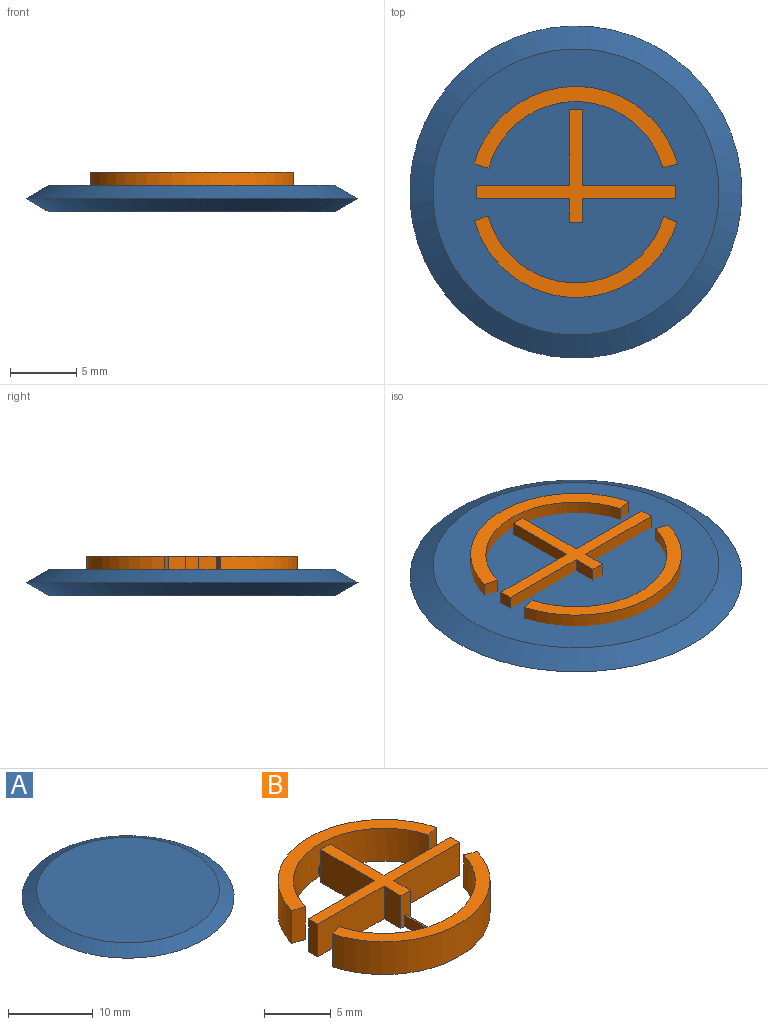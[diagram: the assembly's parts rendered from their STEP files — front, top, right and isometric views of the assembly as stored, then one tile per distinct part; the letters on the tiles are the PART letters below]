
ASSEMBLY  parts=2 mates=1
PART A: 4 faces, bbox 25x25x2 mm
  f0: plane 21.54x21.54mm, normal (0,0,1), area 364.3mm2, adj f1
  f1: cone r=12.5mm half-angle=60deg, axis (0,0,-1), area 146.2mm2, adj f0,f2
  f2: cone r=12.5mm half-angle=60deg, axis (0,0,1), area 146.2mm2, adj f1,f3
  f3: plane 21.54x21.54mm, normal (0,0,-1), area 364.3mm2, adj f2
PART B: 30 faces, bbox 15.3x15.9x3 mm
  f0: plane 1x0.59mm, normal (1,0,0), area 0.6mm2, adj f9,f25,f27,f28
  f1: plane 1x0.59mm, normal (-1,0,0), area 0.6mm2, adj f9,f25,f27,f28
  f2: plane 4.56x1mm, normal (-1,0,0), area 4.6mm2, adj f15,f16,f27,f29
  f3: plane 4.56x1mm, normal (1,0,0), area 4.6mm2, adj f15,f16,f27,f29
  f4: plane 15.25x6.11mm, normal (0,0,1), area 20.9mm2, adj f16,f17,f18,f19
  f5: plane 15x8.5mm, normal (0,0,1), area 22.5mm2, adj f10,f11,f12,f13,f14,f15,f20,f21
  f6: plane 3x1.12mm, normal (0.23,-0.97,0), area 3.4mm2, adj f7,f9,f26,f27
  f7: cylinder r=7.94mm len=15.32mm, axis (0,0,-1), area 62.1mm2, adj f6,f8,f26,f27
  f8: plane 3x1.1mm, normal (-0.27,-0.96,0), area 3.4mm2, adj f7,f9,f26,f27
  f9: cylinder r=6.8mm len=13.1mm, axis (0,0,-1), area 52.9mm2, adj f0,f1,f6,f8,f26,f27,f28
  f10: plane 5.71x3mm, normal (-1,0,0), area 17.1mm2, adj f5,f11,f25,f27
  f11: plane 7x3mm, normal (0,1,0), area 21mm2, adj f5,f10,f12,f27
  f12: plane 3x1mm, normal (-1,0,0), area 3mm2, adj f5,f11,f13,f27
  f13: plane 7x3mm, normal (0,-1,0), area 21mm2, adj f5,f12,f14,f27
  f14: plane 3x1.79mm, normal (-1,0,0), area 5.4mm2, adj f5,f13,f15,f27
  f15: plane 3x1mm, normal (0,-1,0), area 2.8mm2, adj f2,f3,f5,f14,f20,f27,f29
  f16: cylinder r=6.85mm len=13.19mm, axis (0,0,-1), area 53.2mm2, adj f2,f3,f4,f17,f19,f27,f29
  f17: plane 3x1.04mm, normal (-0.31,0.95,0), area 3.3mm2, adj f4,f16,f18,f27
  f18: cylinder r=7.94mm len=15.25mm, axis (0,0,-1), area 61.4mm2, adj f4,f17,f19,f27
  f19: plane 3x1.02mm, normal (0.37,0.93,0), area 3.3mm2, adj f4,f16,f18,f27
  f20: plane 3x1.79mm, normal (1,0,0), area 5.4mm2, adj f5,f15,f21,f27
  f21: plane 7x3mm, normal (0,-1,0), area 21mm2, adj f5,f20,f22,f27
  f22: plane 3x1mm, normal (1,0,0), area 3mm2, adj f5,f21,f23,f27
  f23: plane 7x3mm, normal (0,1,0), area 21mm2, adj f5,f22,f24,f27
  f24: plane 5.71x3mm, normal (1,0,0), area 17.1mm2, adj f5,f23,f25,f27
  f25: plane 3x1mm, normal (0,1,0), area 2.8mm2, adj f0,f1,f5,f10,f24,f27,f28
  f26: plane 15.32x6.16mm, normal (0,0,1), area 22mm2, adj f6,f7,f8,f9
  f27: plane 15.88x15.32mm, normal (0,0,-1), area 66.3mm2, adj f0,f1,f2,f3,f6,f7,f8,f9
  f28: plane 0.59x0.18mm, normal (0,0,1), area 0.1mm2, adj f0,f1,f9,f25
  f29: plane 4.56x0.16mm, normal (0,0,1), area 0.7mm2, adj f2,f3,f15,f16
PLACE A t=(-0.01,0.02,0.03)mm
PLACE B t=(-0.01,0.02,0.03)mm
MATE fastened B.f16 <-> A.f1  axis (0,0,-1) through (-0.01,0.02,-0.97)mm
